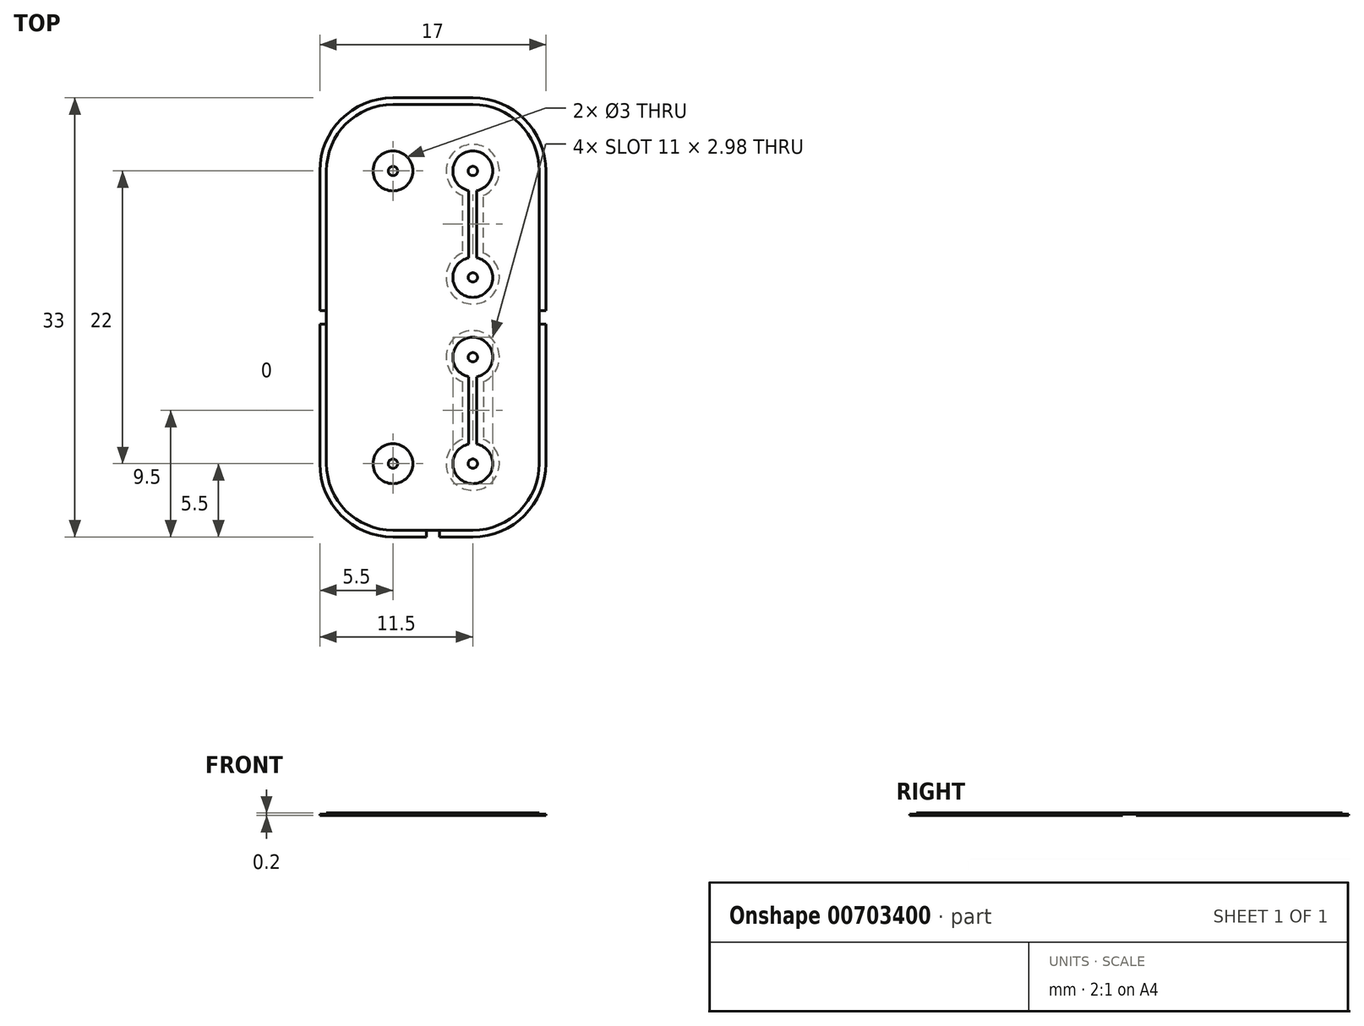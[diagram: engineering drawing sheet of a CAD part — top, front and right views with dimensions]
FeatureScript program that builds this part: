
annotation { "Feature Type Name" : "Feature", "Feature Type Description" : "" }
export const myFeature = defineFeature(function(context is Context, id is Id, definition is map)
    precondition{}
    {
        {
            var Q0;
            Q0=qCreatedBy(makeId("Top.planeOp"),FACE);
            var sketch = newSketch(context, id + "F0", { "sketchPlane" : qUnion([Q0])});
            skLineSegment(sketch, "E0.bottom", {"start": v(0, 0) * mm, "end": v(100, 0) * mm});
            skLineSegment(sketch, "E0.top", {"start": v(0, 70) * mm, "end": v(100, 70) * mm});
            skLineSegment(sketch, "E0.left", {"start": v(0, 0) * mm, "end": v(0, 70) * mm});
            skLineSegment(sketch, "E0.right", {"start": v(100, 0) * mm, "end": v(100, 70) * mm});
            skLineSegment(sketch, "E1.bottom", {"start": v(27, 51) * mm, "end": v(33, 51) * mm});
            skLineSegment(sketch, "E1.top", {"start": v(27, 19) * mm, "end": v(33, 19) * mm});
            skLineSegment(sketch, "E1.left", {"start": v(22, 46) * mm, "end": v(22, 24) * mm});
            skLineSegment(sketch, "E1.right", {"start": v(38, 46) * mm, "end": v(38, 24) * mm});
            skPoint(sketch, "E2.visualSharp", {"position": v(22, 19) * mm});
            skArc(sketch, "E2.filletArc", {"start": v(22, 24) * mm, "mid": v(23.46, 20.46) * mm, "end": v(27, 19) * mm});
            skPoint(sketch, "E3.visualSharp", {"position": v(38, 19) * mm});
            skArc(sketch, "E3.filletArc", {"start": v(33, 19) * mm, "mid": v(36.54, 20.46) * mm, "end": v(38, 24) * mm});
            skPoint(sketch, "E4.visualSharp", {"position": v(38, 51) * mm});
            skArc(sketch, "E4.filletArc", {"start": v(38, 46) * mm, "mid": v(36.54, 49.54) * mm, "end": v(33, 51) * mm});
            skPoint(sketch, "E5.visualSharp", {"position": v(22, 51) * mm});
            skArc(sketch, "E5.filletArc", {"start": v(27, 51) * mm, "mid": v(23.46, 49.54) * mm, "end": v(22, 46) * mm});
            skCircle(sketch, "E6", {"center": v(27, 46) * mm, "radius": 0.35 * mm});
            skCircle(sketch, "E7", {"center": v(33, 46) * mm, "radius": 0.35 * mm});
            skCircle(sketch, "E8", {"center": v(33, 24) * mm, "radius": 0.35 * mm});
            skCircle(sketch, "E9", {"center": v(27, 24) * mm, "radius": 0.35 * mm});
            skCircle(sketch, "E10", {"center": v(33, 38) * mm, "radius": 0.35 * mm});
            skCircle(sketch, "E11", {"center": v(33, 32) * mm, "radius": 0.35 * mm});
            skCircle(sketch, "E12", {"center": v(33, 24) * mm, "radius": 1.5 * mm});
            skCircle(sketch, "E13", {"center": v(33, 32) * mm, "radius": 1.5 * mm});
            skCircle(sketch, "E14", {"center": v(33, 38) * mm, "radius": 1.5 * mm});
            skCircle(sketch, "E15", {"center": v(33, 46) * mm, "radius": 1.5 * mm});
            skCircle(sketch, "E16", {"center": v(33, 46) * mm, "radius": 2 * mm});
            skCircle(sketch, "E17", {"center": v(33, 38) * mm, "radius": 2 * mm});
            skCircle(sketch, "E18", {"center": v(33, 32) * mm, "radius": 2 * mm});
            skCircle(sketch, "E19", {"center": v(33, 24) * mm, "radius": 2 * mm});
            skLineSegment(sketch, "E20.0", {"start": v(27, 51.5) * mm, "end": v(33, 51.5) * mm});
            skArc(sketch, "E20.1", {"start": v(38.5, 46) * mm, "mid": v(36.89, 49.89) * mm, "end": v(33, 51.5) * mm});
            skArc(sketch, "E20.2", {"start": v(27, 51.5) * mm, "mid": v(23.11, 49.89) * mm, "end": v(21.5, 46) * mm});
            skLineSegment(sketch, "E20.3", {"start": v(38.5, 46) * mm, "end": v(38.5, 24) * mm});
            skLineSegment(sketch, "E20.4", {"start": v(21.5, 46) * mm, "end": v(21.5, 24) * mm});
            skArc(sketch, "E20.5", {"start": v(21.5, 24) * mm, "mid": v(23.11, 20.11) * mm, "end": v(27, 18.5) * mm});
            skLineSegment(sketch, "E20.6", {"start": v(27, 18.5) * mm, "end": v(33, 18.5) * mm});
            skArc(sketch, "E20.7", {"start": v(33, 18.5) * mm, "mid": v(36.89, 20.11) * mm, "end": v(38.5, 24) * mm});
            skLineSegment(sketch, "E21", {"start": v(32.2, 44.17) * mm, "end": v(32.2, 39.83) * mm});
            skLineSegment(sketch, "E22", {"start": v(33.8, 39.83) * mm, "end": v(33.8, 44.17) * mm});
            skLineSegment(sketch, "E23", {"start": v(32.7, 44.53) * mm, "end": v(32.7, 39.47) * mm});
            skLineSegment(sketch, "E24", {"start": v(33.3, 44.53) * mm, "end": v(33.3, 39.47) * mm});
            skLineSegment(sketch, "E25", {"start": v(32.2, 30.17) * mm, "end": v(32.2, 25.83) * mm});
            skLineSegment(sketch, "E26", {"start": v(33.8, 30.17) * mm, "end": v(33.8, 25.83) * mm});
            skLineSegment(sketch, "E27", {"start": v(32.7, 30.53) * mm, "end": v(32.7, 25.47) * mm});
            skLineSegment(sketch, "E28", {"start": v(33.3, 30.53) * mm, "end": v(33.3, 25.47) * mm});
            skCircle(sketch, "E29", {"center": v(27, 46) * mm, "radius": 1.5 * mm});
            skCircle(sketch, "E30", {"center": v(27, 24) * mm, "radius": 1.5 * mm});
            skLineSegment(sketch, "E31", {"start": v(21.5, 35.5) * mm, "end": v(22, 35.5) * mm});
            skPoint(sketch, "E31.endSnap0", {"position": v(22, 35) * mm});
            skLineSegment(sketch, "E32", {"start": v(21.5, 34.5) * mm, "end": v(22, 34.5) * mm});
            skLineSegment(sketch, "E33", {"start": v(38, 35.5) * mm, "end": v(38.5, 35.5) * mm});
            skLineSegment(sketch, "E34", {"start": v(38, 34.5) * mm, "end": v(38.5, 34.5) * mm});
            skLineSegment(sketch, "E35", {"start": v(29.5, 51.5) * mm, "end": v(29.5, 51) * mm});
            skLineSegment(sketch, "E36", {"start": v(30.5, 51.5) * mm, "end": v(30.5, 51) * mm});
            skLineSegment(sketch, "E37", {"start": v(29.5, 19) * mm, "end": v(29.5, 18.5) * mm});
            skLineSegment(sketch, "E38", {"start": v(30.5, 19) * mm, "end": v(30.5, 18.5) * mm});
            skLineSegment(sketch, "E39.bottom", {"start": v(29.5, 19) * mm, "end": v(30.5, 19) * mm});
            skLineSegment(sketch, "E39.top", {"start": v(29.5, 18.5) * mm, "end": v(30.5, 18.5) * mm});
            skPoint(sketch, "E39.middle", {"position": v(30, 18.75) * mm});
            skPoint(sketch, "E39.middle.positionSnap0", {"position": v(30, 18.5) * mm});
            skPoint(sketch, "E39.centerSnap0", {"position": v(30, 18.5) * mm});
            skLineSegment(sketch, "E40", {"start": v(30, 70) * mm, "end": v(30, 0) * mm, "construction": true});
            skLineSegment(sketch, "E41", {"start": v(0, 35) * mm, "end": v(100, 35) * mm, "construction": true});
            skSolve(sketch);
        }
        {
            var Q0;
            {var subQ3=sQuery(id+"F0.wireOp",EDGE,"E27");var subQ4=sQuery(id+"F0.wireOp",EDGE,"E12");var subQ5=makeQuery(id+"F0.imprint","INTERSECT",VERTEX,{"derivedFrom":[subQ4,subQ3]});Q0=makeQuery(id+"F0.imprint","IMPRINT",FACE,{"disambiguationData":[TD([[makeQuery(id+"F0.imprint","IMPRINT",EDGE,{"disambiguationData":[TD([[subQ5,-1.0]])],"derivedFrom":subQ4}),-1.0]])]});}
            var Q1;
            {var subQ0=sQuery(id+"F0.wireOp",EDGE,"E25");Q1=makeQuery(id+"F0.imprint","IMPRINT",FACE,{"disambiguationData":[TD([[makeQuery(id+"F0.imprint","IMPRINT",EDGE,{"derivedFrom":subQ0}),1.0]])]});}
            var Q2;
            {var subQ3=sQuery(id+"F0.wireOp",EDGE,"E27");var subQ7=sQuery(id+"F0.wireOp",EDGE,"E13");var subQ8=makeQuery(id+"F0.imprint","INTERSECT",VERTEX,{"derivedFrom":[subQ7,subQ3]});Q2=makeQuery(id+"F0.imprint","IMPRINT",FACE,{"disambiguationData":[TD([[makeQuery(id+"F0.imprint","IMPRINT",EDGE,{"disambiguationData":[TD([[subQ8,1.0]])],"derivedFrom":subQ7}),-1.0]])]});}
            var Q3;
            {var subQ0=sQuery(id+"F0.wireOp",EDGE,"E26");Q3=makeQuery(id+"F0.imprint","IMPRINT",FACE,{"disambiguationData":[TD([[makeQuery(id+"F0.imprint","IMPRINT",EDGE,{"derivedFrom":subQ0}),-1.0]])]});}
            var Q4;
            {var subQ2=sQuery(id+"F0.wireOp",EDGE,"E23");var subQ4=sQuery(id+"F0.wireOp",EDGE,"E14");var subQ5=makeQuery(id+"F0.imprint","INTERSECT",VERTEX,{"derivedFrom":[subQ4,subQ2]});Q4=makeQuery(id+"F0.imprint","IMPRINT",FACE,{"disambiguationData":[TD([[makeQuery(id+"F0.imprint","IMPRINT",EDGE,{"disambiguationData":[TD([[subQ5,-1.0]])],"derivedFrom":subQ4}),-1.0]])]});}
            var Q5;
            {var subQ0=sQuery(id+"F0.wireOp",EDGE,"E21");Q5=makeQuery(id+"F0.imprint","IMPRINT",FACE,{"disambiguationData":[TD([[makeQuery(id+"F0.imprint","IMPRINT",EDGE,{"derivedFrom":subQ0}),1.0]])]});}
            var Q6;
            {var subQ5=sQuery(id+"F0.wireOp",EDGE,"E23");var subQ7=sQuery(id+"F0.wireOp",EDGE,"E15");var subQ8=makeQuery(id+"F0.imprint","INTERSECT",VERTEX,{"derivedFrom":[subQ7,subQ5]});Q6=makeQuery(id+"F0.imprint","IMPRINT",FACE,{"disambiguationData":[TD([[makeQuery(id+"F0.imprint","IMPRINT",EDGE,{"disambiguationData":[TD([[subQ8,1.0]])],"derivedFrom":subQ7}),-1.0]])]});}
            var Q7;
            {var subQ0=sQuery(id+"F0.wireOp",EDGE,"E22");Q7=makeQuery(id+"F0.imprint","IMPRINT",FACE,{"disambiguationData":[TD([[makeQuery(id+"F0.imprint","IMPRINT",EDGE,{"derivedFrom":subQ0}),1.0]])]});}
            extrude(context, id + "F1", {"entities" : qUnion([Q0, Q1, Q2, Q3, Q4, Q5, Q6, Q7]), "oppositeDirection" : true, "depth" : .1 * mm, "offsetDistance" : 25 * mm});
        }
        {
            var Q0;
            {var subQ3=sQuery(id+"F0.wireOp",EDGE,"E5.filletArc");Q0=makeQuery(id+"F0.imprint","IMPRINT",FACE,{"disambiguationData":[TD([[makeQuery(id+"F0.imprint","IMPRINT",EDGE,{"derivedFrom":subQ3}),-1.0]])]});}
            var Q1;
            {var subQ1=sQuery(id+"F0.wireOp",EDGE,"E4.filletArc");Q1=makeQuery(id+"F0.imprint","IMPRINT",FACE,{"disambiguationData":[TD([[makeQuery(id+"F0.imprint","IMPRINT",EDGE,{"derivedFrom":subQ1}),-1.0]])]});}
            var Q2;
            {var subQ3=sQuery(id+"F0.wireOp",EDGE,"E2.filletArc");Q2=makeQuery(id+"F0.imprint","IMPRINT",FACE,{"disambiguationData":[TD([[makeQuery(id+"F0.imprint","IMPRINT",EDGE,{"derivedFrom":subQ3}),-1.0]])]});}
            var Q3;
            {var subQ1=sQuery(id+"F0.wireOp",EDGE,"E3.filletArc");Q3=makeQuery(id+"F0.imprint","IMPRINT",FACE,{"disambiguationData":[TD([[makeQuery(id+"F0.imprint","IMPRINT",EDGE,{"derivedFrom":subQ1}),-1.0]])]});}
            var Q4;
            Q4=makeQuery(id+"F0.imprint","IMPRINT",FACE,{"disambiguationData":[TD([[makeQuery(id+"F0.imprint","IMPRINT",EDGE,{"derivedFrom":sQuery(id+"F0.wireOp",EDGE,"E39.bottom")}),-1.0]])]});
            var Q5;
            {var subQ0=sQuery(id+"F0.wireOp",EDGE,"E35");Q5=makeQuery(id+"F0.imprint","IMPRINT",FACE,{"disambiguationData":[TD([[makeQuery(id+"F0.imprint","IMPRINT",EDGE,{"derivedFrom":subQ0}),1.0]])]});}
            extrude(context, id + "F2", {"entities" : qUnion([Q0, Q1, Q2, Q3, Q4, Q5]), "oppositeDirection" : true, "depth" : .1 * mm, "offsetDistance" : 25 * mm});
        }
        {
            var Q0;
            Q0=makeQuery(id+"F0.imprint","IMPRINT",FACE,{"disambiguationData":[TD([[makeQuery(id+"F0.imprint","IMPRINT",EDGE,{"derivedFrom":sQuery(id+"F0.wireOp",EDGE,"E7")}),1.0]])]});
            var Q1;
            Q1=makeQuery(id+"F0.imprint","IMPRINT",FACE,{"disambiguationData":[TD([[makeQuery(id+"F0.imprint","IMPRINT",EDGE,{"derivedFrom":sQuery(id+"F0.wireOp",EDGE,"E10")}),1.0]])]});
            var Q2;
            Q2=makeQuery(id+"F0.imprint","IMPRINT",FACE,{"disambiguationData":[TD([[makeQuery(id+"F0.imprint","IMPRINT",EDGE,{"derivedFrom":sQuery(id+"F0.wireOp",EDGE,"E11")}),1.0]])]});
            var Q3;
            Q3=makeQuery(id+"F0.imprint","IMPRINT",FACE,{"disambiguationData":[TD([[makeQuery(id+"F0.imprint","IMPRINT",EDGE,{"derivedFrom":sQuery(id+"F0.wireOp",EDGE,"E8")}),1.0]])]});
            var Q4;
            Q4=makeQuery(id+"F0.imprint","IMPRINT",FACE,{"disambiguationData":[TD([[makeQuery(id+"F0.imprint","IMPRINT",EDGE,{"derivedFrom":sQuery(id+"F0.wireOp",EDGE,"E9")}),1.0]])]});
            var Q5;
            Q5=makeQuery(id+"F0.imprint","IMPRINT",FACE,{"disambiguationData":[TD([[makeQuery(id+"F0.imprint","IMPRINT",EDGE,{"derivedFrom":sQuery(id+"F0.wireOp",EDGE,"E6")}),1.0]])]});
            extrude(context, id + "F3", {"entities" : qUnion([Q0, Q1, Q2, Q3, Q4, Q5]), "oppositeDirection" : true, "depth" : .1 * mm, "offsetDistance" : 25 * mm});
        }
        {
            var Q0;
            Q0=makeQuery(id+"F0.imprint","IMPRINT",FACE,{"disambiguationData":[TD([[makeQuery(id+"F0.imprint","IMPRINT",EDGE,{"derivedFrom":sQuery(id+"F0.wireOp",EDGE,"E1.bottom")}),-1.0]])]});
            var Q1;
            {var subQ5=sQuery(id+"F0.wireOp",EDGE,"E23");var subQ7=sQuery(id+"F0.wireOp",EDGE,"E15");var subQ8=makeQuery(id+"F0.imprint","INTERSECT",VERTEX,{"derivedFrom":[subQ7,subQ5]});Q1=makeQuery(id+"F0.imprint","IMPRINT",FACE,{"disambiguationData":[TD([[makeQuery(id+"F0.imprint","IMPRINT",EDGE,{"disambiguationData":[TD([[subQ8,1.0]])],"derivedFrom":subQ7}),-1.0]])]});}
            var Q2;
            {var subQ0=sQuery(id+"F0.wireOp",EDGE,"E21");Q2=makeQuery(id+"F0.imprint","IMPRINT",FACE,{"disambiguationData":[TD([[makeQuery(id+"F0.imprint","IMPRINT",EDGE,{"derivedFrom":subQ0}),1.0]])]});}
            var Q3;
            {var subQ0=sQuery(id+"F0.wireOp",EDGE,"E22");Q3=makeQuery(id+"F0.imprint","IMPRINT",FACE,{"disambiguationData":[TD([[makeQuery(id+"F0.imprint","IMPRINT",EDGE,{"derivedFrom":subQ0}),1.0]])]});}
            var Q4;
            {var subQ2=sQuery(id+"F0.wireOp",EDGE,"E23");var subQ4=sQuery(id+"F0.wireOp",EDGE,"E14");var subQ5=makeQuery(id+"F0.imprint","INTERSECT",VERTEX,{"derivedFrom":[subQ4,subQ2]});Q4=makeQuery(id+"F0.imprint","IMPRINT",FACE,{"disambiguationData":[TD([[makeQuery(id+"F0.imprint","IMPRINT",EDGE,{"disambiguationData":[TD([[subQ5,-1.0]])],"derivedFrom":subQ4}),-1.0]])]});}
            var Q5;
            {var subQ3=sQuery(id+"F0.wireOp",EDGE,"E27");var subQ7=sQuery(id+"F0.wireOp",EDGE,"E13");var subQ8=makeQuery(id+"F0.imprint","INTERSECT",VERTEX,{"derivedFrom":[subQ7,subQ3]});Q5=makeQuery(id+"F0.imprint","IMPRINT",FACE,{"disambiguationData":[TD([[makeQuery(id+"F0.imprint","IMPRINT",EDGE,{"disambiguationData":[TD([[subQ8,1.0]])],"derivedFrom":subQ7}),-1.0]])]});}
            var Q6;
            {var subQ0=sQuery(id+"F0.wireOp",EDGE,"E25");Q6=makeQuery(id+"F0.imprint","IMPRINT",FACE,{"disambiguationData":[TD([[makeQuery(id+"F0.imprint","IMPRINT",EDGE,{"derivedFrom":subQ0}),1.0]])]});}
            var Q7;
            {var subQ0=sQuery(id+"F0.wireOp",EDGE,"E26");Q7=makeQuery(id+"F0.imprint","IMPRINT",FACE,{"disambiguationData":[TD([[makeQuery(id+"F0.imprint","IMPRINT",EDGE,{"derivedFrom":subQ0}),-1.0]])]});}
            var Q8;
            {var subQ3=sQuery(id+"F0.wireOp",EDGE,"E27");var subQ4=sQuery(id+"F0.wireOp",EDGE,"E12");var subQ5=makeQuery(id+"F0.imprint","INTERSECT",VERTEX,{"derivedFrom":[subQ4,subQ3]});Q8=makeQuery(id+"F0.imprint","IMPRINT",FACE,{"disambiguationData":[TD([[makeQuery(id+"F0.imprint","IMPRINT",EDGE,{"disambiguationData":[TD([[subQ5,-1.0]])],"derivedFrom":subQ4}),-1.0]])]});}
            extrude(context, id + "F4", {"entities" : qUnion([Q0, Q1, Q2, Q3, Q4, Q5, Q6, Q7, Q8]), "depth" : .1 * mm, "offsetDistance" : 25 * mm});
        }
    });
